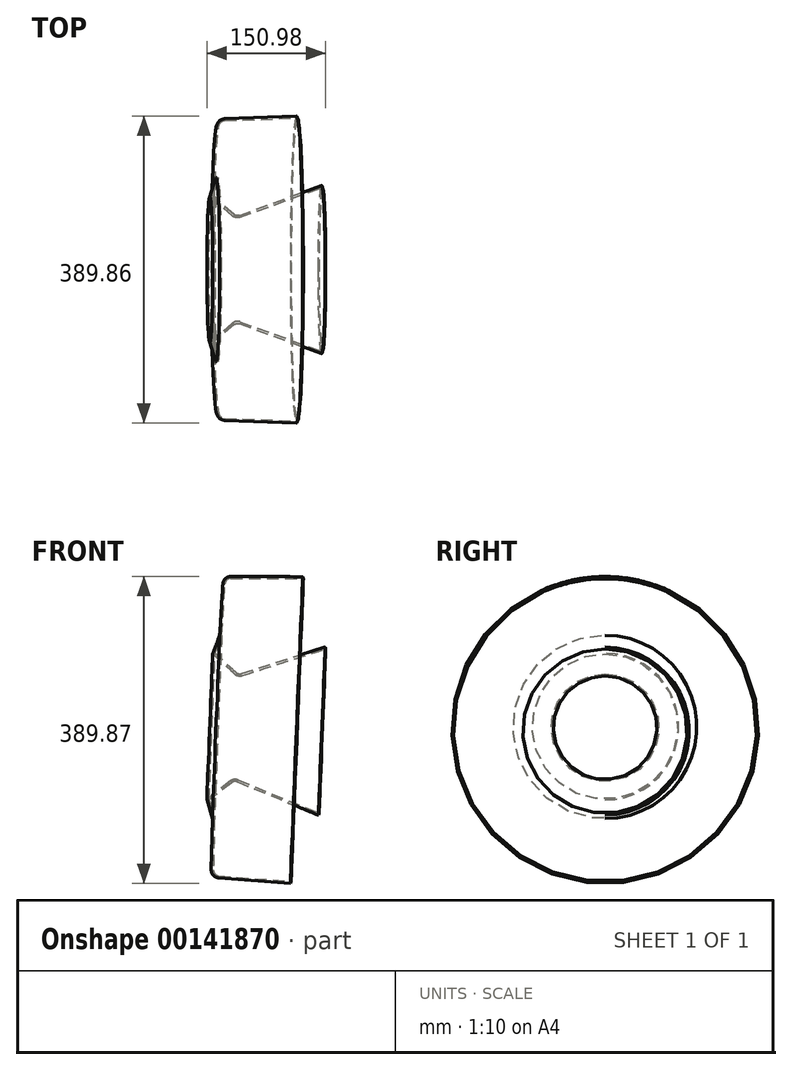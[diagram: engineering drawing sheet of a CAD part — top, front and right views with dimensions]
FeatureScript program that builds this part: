
annotation { "Feature Type Name" : "Feature", "Feature Type Description" : "" }
export const myFeature = defineFeature(function(context is Context, id is Id, definition is map)
    precondition{}
    {
        {
            var Q0;
            Q0=qCreatedBy(makeId("Front.planeOp"),FACE);
            var sketch = newSketch(context, id + "F0", { "sketchPlane" : qUnion([Q0])});
            skLineSegment(sketch, "E0", {"start": v(-133.58, -19.97) * mm, "end": v(-129.7, 44.7) * mm});
            skLineSegment(sketch, "E1", {"start": v(-119.68, 54.1) * mm, "end": v(-28.24, 53.78) * mm});
            skLineSegment(sketch, "E2", {"start": v(-28.24, 53.78) * mm, "end": v(0.98, -37.97) * mm});
            skLineSegment(sketch, "E3", {"start": v(0.98, -37.97) * mm, "end": v(-104.94, -71.7) * mm});
            skLineSegment(sketch, "E4", {"start": v(-114.71, -69.57) * mm, "end": v(-142.52, -44.2) * mm});
            skLineSegment(sketch, "E5", {"start": v(-142.52, -44.2) * mm, "end": v(-133.58, -19.97) * mm});
            skPoint(sketch, "E6.visualSharp", {"position": v(-129.14, 54.14) * mm});
            skArc(sketch, "E6.filletArc", {"start": v(-119.68, 54.1) * mm, "mid": v(-126.56, 51.4) * mm, "end": v(-129.7, 44.7) * mm});
            skPoint(sketch, "E7.visualSharp", {"position": v(-110.45, -73.46) * mm});
            skArc(sketch, "E7.filletArc", {"start": v(-114.71, -69.57) * mm, "mid": v(-110.11, -71.95) * mm, "end": v(-104.94, -71.7) * mm});
            skLineSegment(sketch, "E8", {"start": v(-176.27, -135.33) * mm, "end": v(48.56, -144.42) * mm, "construction": true});
            skSolve(sketch);
        }
        {
            var Q0;
            Q0 = qSketchRegion(id + "F0", true);
            var Q1;
            Q1=sQuery(id+"F0.wireOp",EDGE,"E8");
            revolve(context, id + "F1", {"entities" : qUnion([Q0]), "axis" : qUnion([Q1]), "revolveType" : RevolveType.FULL});
        }
        {
            var Q0;
            Q0=makeQuery(id+"F1.opRevolve","SWEPT_FACE",FACE,{"disambiguationData":[OSD([sQuery(id+"F0.wireOp",EDGE,"E2")])]});
            shell(context, id + "F2", {"entities" : qUnion([Q0]), "thickness" : 2.5 * mm});
        }
    });
